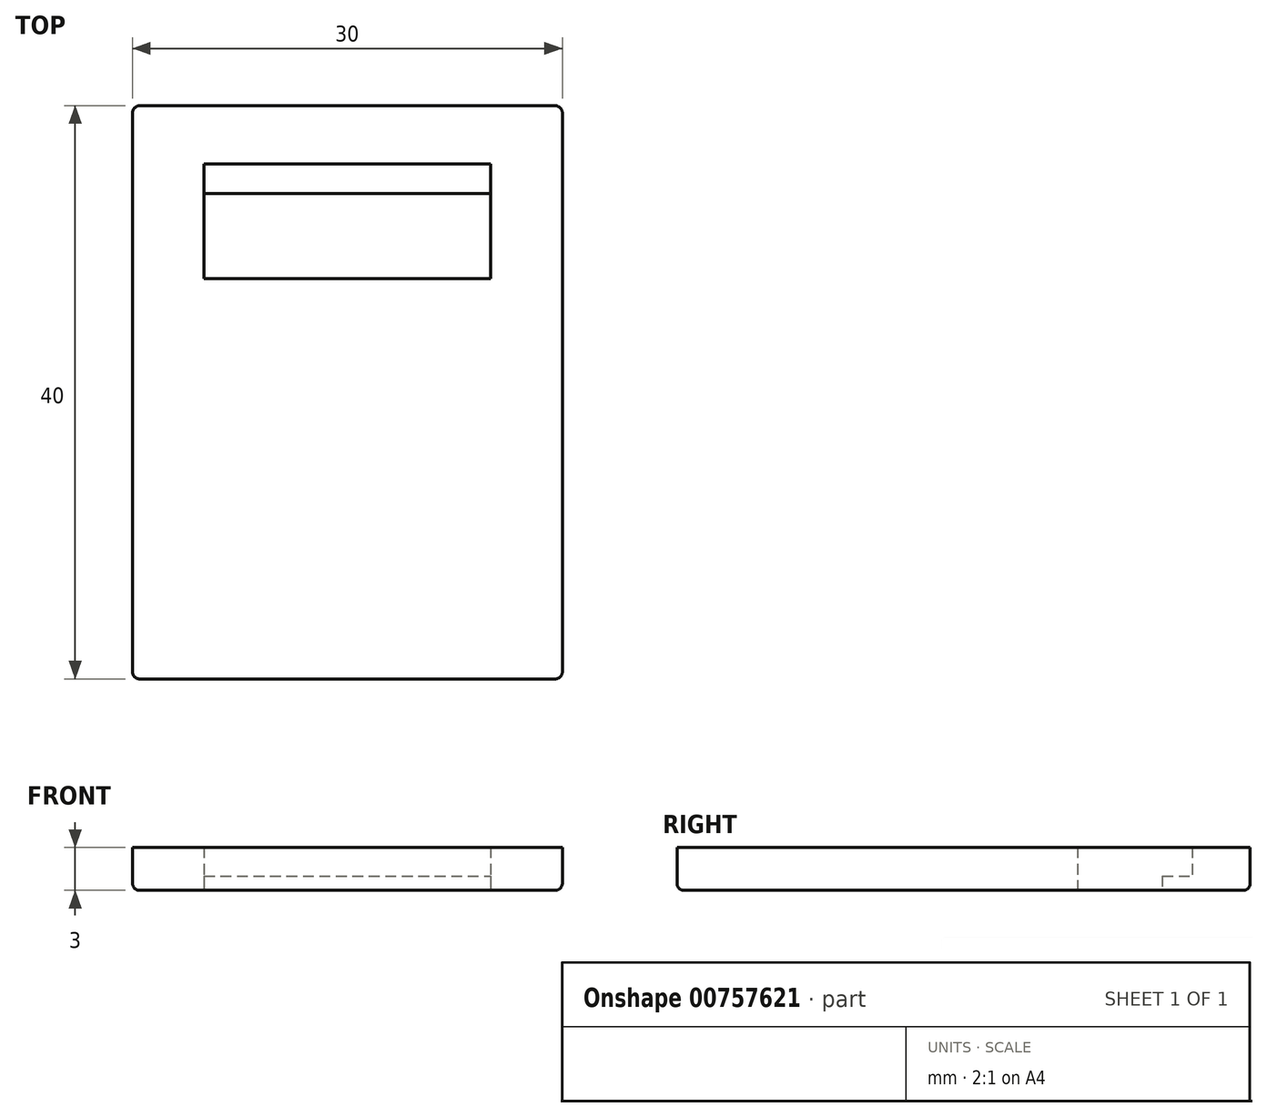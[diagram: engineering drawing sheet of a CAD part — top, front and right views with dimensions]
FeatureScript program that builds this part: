
annotation { "Feature Type Name" : "Feature", "Feature Type Description" : "" }
export const myFeature = defineFeature(function(context is Context, id is Id, definition is map)
    precondition{}
    {
        {
            var Q0;
            Q0=qCreatedBy(makeId("Top.planeOp"),FACE);
            var sketch = newSketch(context, id + "F0", { "sketchPlane" : qUnion([Q0])});
            skLineSegment(sketch, "E0.bottom", {"start": v(-15, 20) * mm, "end": v(15, 20) * mm});
            skLineSegment(sketch, "E0.top", {"start": v(-15, -20) * mm, "end": v(15, -20) * mm});
            skLineSegment(sketch, "E0.left", {"start": v(-15, 20) * mm, "end": v(-15, -20) * mm});
            skLineSegment(sketch, "E0.right", {"start": v(15, 20) * mm, "end": v(15, -20) * mm});
            skPoint(sketch, "E0.middle", {"position": v(0, 0) * mm});
            skLineSegment(sketch, "E1.bottom", {"start": v(-10, 15.94) * mm, "end": v(10, 15.94) * mm});
            skLineSegment(sketch, "E1.top", {"start": v(-10, 7.94) * mm, "end": v(10, 7.94) * mm});
            skLineSegment(sketch, "E1.left", {"start": v(-10, 15.94) * mm, "end": v(-10, 7.94) * mm});
            skLineSegment(sketch, "E1.right", {"start": v(10, 15.94) * mm, "end": v(10, 7.94) * mm});
            skPoint(sketch, "E1.middle", {"position": v(0, 11.94) * mm});
            skSolve(sketch);
        }
        {
            var Q0;
            Q0=makeQuery(id+"F0.imprint","IMPRINT",FACE,{"disambiguationData":[TD([[makeQuery(id+"F0.imprint","IMPRINT",EDGE,{"derivedFrom":sQuery(id+"F0.wireOp",EDGE,"E0.bottom")}),-1.0]])]});
            var sketch = newSketch(context, id + "F1", { "sketchPlane" : qUnion([Q0])});
            skLineSegment(sketch, "E2.bottom", {"start": v(-10, 13.87) * mm, "end": v(10, 13.87) * mm});
            skLineSegment(sketch, "E2.top", {"start": v(-10, 16.87) * mm, "end": v(10, 16.87) * mm});
            skLineSegment(sketch, "E2.left", {"start": v(-10, 13.87) * mm, "end": v(-10, 16.87) * mm});
            skLineSegment(sketch, "E2.right", {"start": v(10, 13.87) * mm, "end": v(10, 16.87) * mm});
            skPoint(sketch, "E2.middle", {"position": v(0, 15.37) * mm});
            skSolve(sketch);
        }
        {
            var Q0;
            Q0 = qSketchRegion(id + "F0", true);
            extrude(context, id + "F2", {"entities" : qUnion([Q0]), "depth" : 3 * mm, "offsetDistance" : 25 * mm});
        }
        {
            var Q0;
            Q0 = qSketchRegion(id + "F1", true);
            extrude(context, id + "F3", {"entities" : qUnion([Q0]), "operationType" : NewBodyOperationType.ADD, "depth" : 1 * mm, "offsetDistance" : 25 * mm});
        }
        {
            var Q0;
            Q0=makeQuery(id+"F2.opExtrude","CAP_EDGE",EDGE,{"disambiguationData":[OSD([sQuery(id+"F0.wireOp",EDGE,"E0.right")])],"isStart":true});
            var Q1;
            Q1=makeQuery(id+"F2.opExtrude","CAP_EDGE",EDGE,{"disambiguationData":[OSD([sQuery(id+"F0.wireOp",EDGE,"E0.bottom")])],"isStart":true});
            var Q2;
            Q2=makeQuery(id+"F2.opExtrude","CAP_EDGE",EDGE,{"disambiguationData":[OSD([sQuery(id+"F0.wireOp",EDGE,"E0.left")])],"isStart":true});
            var Q3;
            Q3=makeQuery(id+"F2.opExtrude","CAP_EDGE",EDGE,{"disambiguationData":[OSD([sQuery(id+"F0.wireOp",EDGE,"E0.top")])],"isStart":true});
            var Q4;
            Q4=makeQuery(id+"F2.opExtrude","SWEPT_EDGE",EDGE,{"disambiguationData":[OSD([sQuery(id+"F0.wireOp",EDGE,"E0.top"),sQuery(id+"F0.wireOp",EDGE,"E0.left")])]});
            var Q5;
            Q5=makeQuery(id+"F2.opExtrude","SWEPT_EDGE",EDGE,{"disambiguationData":[OSD([sQuery(id+"F0.wireOp",EDGE,"E0.top"),sQuery(id+"F0.wireOp",EDGE,"E0.right")])]});
            var Q6;
            Q6=makeQuery(id+"F2.opExtrude","SWEPT_EDGE",EDGE,{"disambiguationData":[OSD([sQuery(id+"F0.wireOp",EDGE,"E0.bottom"),sQuery(id+"F0.wireOp",EDGE,"E0.left")])]});
            var Q7;
            Q7=makeQuery(id+"F2.opExtrude","SWEPT_EDGE",EDGE,{"disambiguationData":[OSD([sQuery(id+"F0.wireOp",EDGE,"E0.bottom"),sQuery(id+"F0.wireOp",EDGE,"E0.right")])]});
            fillet(context, id + "F4", {"entities" : qUnion([Q0, Q1, Q2, Q3, Q4, Q5, Q6, Q7]), "radius" : 0.5 * mm, "tangentPropagation" : true, "allowEdgeOverflow" : false});
        }
    });
